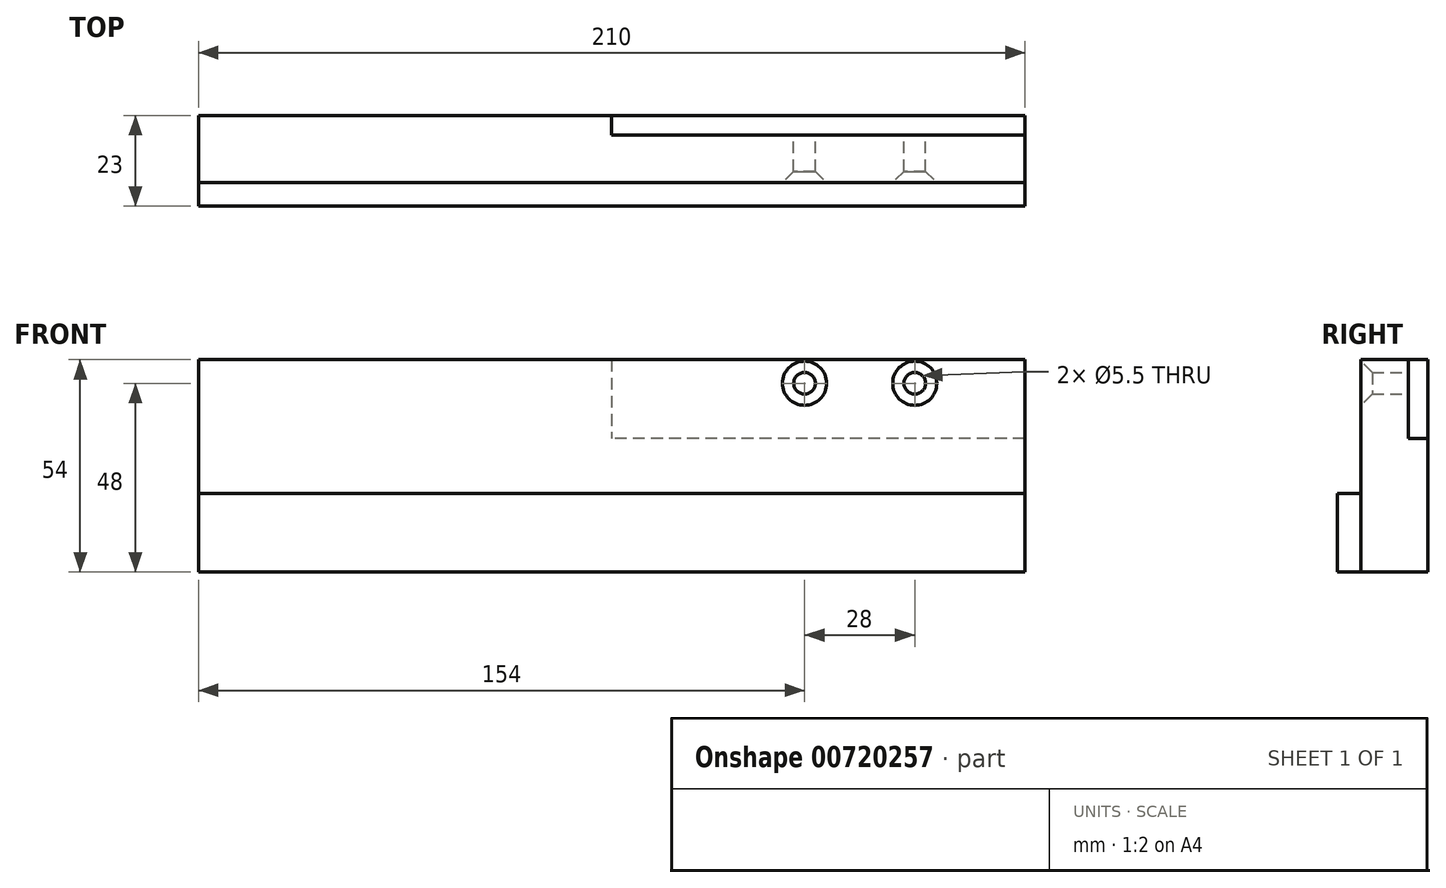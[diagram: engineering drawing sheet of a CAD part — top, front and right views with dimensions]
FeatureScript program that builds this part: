
annotation { "Feature Type Name" : "Feature", "Feature Type Description" : "" }
export const myFeature = defineFeature(function(context is Context, id is Id, definition is map)
    precondition{}
    {
        {
            var Q0;
            Q0=qCreatedBy(makeId("Front.planeOp"),FACE);
            var sketch = newSketch(context, id + "F0", { "sketchPlane" : qUnion([Q0])});
            skLineSegment(sketch, "E0.bottom", {"start": v(105, 27) * mm, "end": v(-105, 27) * mm});
            skLineSegment(sketch, "E0.top", {"start": v(105, -27) * mm, "end": v(-105, -27) * mm});
            skLineSegment(sketch, "E0.left", {"start": v(105, 27) * mm, "end": v(105, -27) * mm});
            skLineSegment(sketch, "E0.right", {"start": v(-105, 27) * mm, "end": v(-105, -27) * mm});
            skPoint(sketch, "E0.middle", {"position": v(0, 0) * mm});
            skPoint(sketch, "E1", {"position": v(77, 21) * mm});
            skPoint(sketch, "E2", {"position": v(49, 21) * mm});
            skSolve(sketch);
        }
        {
            var Q0;
            Q0=makeQuery(id+"F0.imprint","IMPRINT",FACE,{"disambiguationData":[TD([[makeQuery(id+"F0.imprint","IMPRINT",EDGE,{"derivedFrom":sQuery(id+"F0.wireOp",EDGE,"E0.bottom")}),1.0]])]});
            extrude(context, id + "F1", {"entities" : qUnion([Q0]), "depth" : 12 * mm, "offsetDistance" : 25 * mm});
        }
        {
            var Q0;
            Q0=makeQuery(id+"F1.opExtrude","CAP_FACE",FACE,{"disambiguationData":[OSD([sQuery(id+"F0.wireOp",EDGE,"E0.bottom"),sQuery(id+"F0.wireOp",EDGE,"E0.top"),sQuery(id+"F0.wireOp",EDGE,"E0.left"),sQuery(id+"F0.wireOp",EDGE,"E0.right"),sQuery(id+"F0.wireOp",EDGE,"tJaZeCe4-3PW8-KLJq-PU98-8hqSa4SxqoTw"),sQuery(id+"F0.wireOp",EDGE,"V6ilIFJ5-Na6r-DEEM-nDBO-AS7CgAQQ2qPl"),sQuery(id+"F0.wireOp",EDGE,"EMkVk4Yk-1Rpp-KUze-79Ad-I5bPLghq1z1C"),sQuery(id+"F0.wireOp",EDGE,"CwgF2355-fNpO-t29W-RsF7-yWW2Hr6mnxz2"),sQuery(id+"F0.wireOp",EDGE,"JxT7Y64N-WG92-Sh1A-dJ0r-4Iu21h3hCUTo"),sQuery(id+"F0.wireOp",EDGE,"uoBUNw4c-wX9n-ujas-8r4R-zFZlIjbgpvJF"),sQuery(id+"F0.wireOp",EDGE,"J2epXsHX-k77t-XQEk-yU51-tST1f28O67I1"),sQuery(id+"F0.wireOp",EDGE,"PYFIOfYx-wvzl-ewAh-qvdA-9tWrAVaHGwcV")])],"isStart":true});
            var sketch = newSketch(context, id + "F2", { "sketchPlane" : qUnion([Q0])});
            skLineSegment(sketch, "E3.bottom", {"start": v(-105, 27) * mm, "end": v(0, 27) * mm});
            skLineSegment(sketch, "E3.top", {"start": v(-105, 7) * mm, "end": v(0, 7) * mm});
            skLineSegment(sketch, "E3.left", {"start": v(-105, 27) * mm, "end": v(-105, 7) * mm});
            skLineSegment(sketch, "E3.right", {"start": v(0, 27) * mm, "end": v(0, 7) * mm});
            skSolve(sketch);
        }
        {
            var Q0;
            {var subQ4=sQuery(id+"F2.wireOp",EDGE,"E3.top");Q0=makeQuery(id+"F2.imprint","IMPRINT",FACE,{"disambiguationData":[TD([[makeQuery(id+"F2.imprint","IMPRINT",EDGE,{"derivedFrom":subQ4}),-1.0]])]});}
            extrude(context, id + "F3", {"entities" : qUnion([Q0]), "operationType" : NewBodyOperationType.ADD, "depth" : 5 * mm, "offsetDistance" : 25 * mm});
        }
        {
            var Q0;
            Q0=makeQuery(id+"F1.opExtrude","CAP_FACE",FACE,{"disambiguationData":[OSD([sQuery(id+"F0.wireOp",EDGE,"E0.bottom"),sQuery(id+"F0.wireOp",EDGE,"E0.top"),sQuery(id+"F0.wireOp",EDGE,"E0.left"),sQuery(id+"F0.wireOp",EDGE,"E0.right")])],"isStart":false});
            var sketch = newSketch(context, id + "F4", { "sketchPlane" : qUnion([Q0])});
            skPoint(sketch, "E4.0", {"position": v(49, 21) * mm});
            skPoint(sketch, "E5.0", {"position": v(77, 21) * mm});
            skSolve(sketch);
        }
        {
            var Q0;
            Q0=sQuery(id+"F4.wireOp",VERTEX,"E4.0");
            var Q1;
            Q1=sQuery(id+"F4.wireOp",VERTEX,"E5.0");
            var Q2;
            Q2=makeQuery(id+"F1.opExtrude","SWEPT_BODY",BODY,{"disambiguationData":[OSD([sQuery(id+"F0.wireOp",EDGE,"E0.bottom"),sQuery(id+"F0.wireOp",EDGE,"E0.top"),sQuery(id+"F0.wireOp",EDGE,"E0.left"),sQuery(id+"F0.wireOp",EDGE,"E0.right")])]});
            hole(context, id + "F5", {"style" : HoleStyle.C_SINK, "endStyle" : HoleEndStyle.THROUGH, "standardTappedOrClearance" : lookupTablePath({ "fit" : "Normal", "standard" : "ISO", "size" : "M5", "type" : "Clearance" }), "standardBlindInLast" : lookupTablePath({ "fit" : "Standard", "standard" : "ISO", "size" : "M5", "type" : "Clearance" }), "holeDiameter" : 5.5 * mm, "cSinkDiameter" : 11.2 * mm, "cSinkAngle" : 90 * degree, "majorDiameter" : 5 * mm, "tappedDepth" : 12 * mm, "tapClearance" : 3, "startFromSketch" : true, "locations" : qUnion([Q0, Q1]), "scope" : qUnion([Q2])});
        }
        {
            var Q0;
            Q0=makeQuery(id+"F1.opExtrude","CAP_FACE",FACE,{"disambiguationData":[OSD([sQuery(id+"F0.wireOp",EDGE,"E0.bottom"),sQuery(id+"F0.wireOp",EDGE,"E0.top"),sQuery(id+"F0.wireOp",EDGE,"E0.left"),sQuery(id+"F0.wireOp",EDGE,"E0.right")])],"isStart":false});
            var sketch = newSketch(context, id + "F6", { "sketchPlane" : qUnion([Q0])});
            skLineSegment(sketch, "E6.bottom", {"start": v(-105, -27) * mm, "end": v(105, -27) * mm});
            skLineSegment(sketch, "E6.top", {"start": v(-105, -7) * mm, "end": v(105, -7) * mm});
            skLineSegment(sketch, "E6.left", {"start": v(-105, -27) * mm, "end": v(-105, -7) * mm});
            skLineSegment(sketch, "E6.right", {"start": v(105, -27) * mm, "end": v(105, -7) * mm});
            skSolve(sketch);
        }
        {
            var Q0;
            Q0=makeQuery(id+"F6.imprint","IMPRINT",FACE,{"disambiguationData":[TD([[makeQuery(id+"F6.imprint","IMPRINT",EDGE,{"derivedFrom":sQuery(id+"F6.wireOp",EDGE,"E6.bottom")}),-1.0]])]});
            extrude(context, id + "F7", {"entities" : qUnion([Q0]), "depth" : 6 * mm, "offsetDistance" : 25 * mm});
        }
    });
